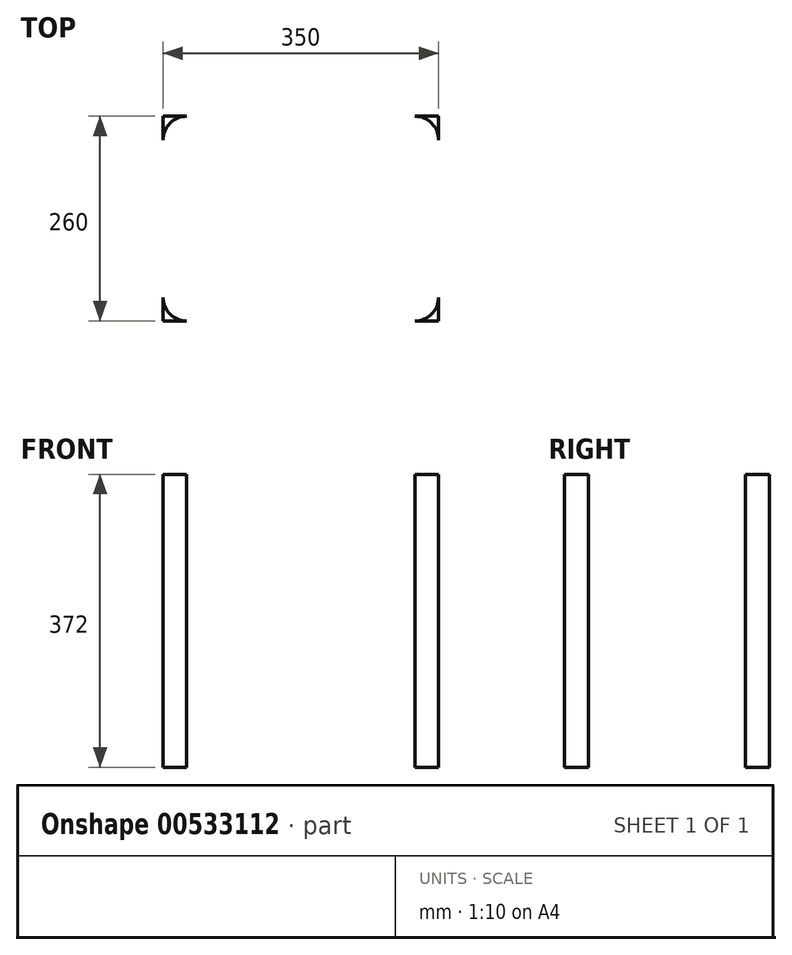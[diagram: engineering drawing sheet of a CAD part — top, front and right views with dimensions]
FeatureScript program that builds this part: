
annotation { "Feature Type Name" : "Feature", "Feature Type Description" : "" }
export const myFeature = defineFeature(function(context is Context, id is Id, definition is map)
    precondition{}
    {
        {
            var Q0;
            Q0=qCreatedBy(makeId("Top.planeOp"),FACE);
            var sketch = newSketch(context, id + "F0", { "sketchPlane" : qUnion([Q0])});
            skLineSegment(sketch, "E0.bottom", {"start": v(0, 260) * mm, "end": v(350, 260) * mm, "construction": true});
            skLineSegment(sketch, "E0.top", {"start": v(0, 0) * mm, "end": v(350, 0) * mm, "construction": true});
            skLineSegment(sketch, "E0.left", {"start": v(0, 260) * mm, "end": v(0, 0) * mm, "construction": true});
            skLineSegment(sketch, "E0.right", {"start": v(350, 260) * mm, "end": v(350, 0) * mm, "construction": true});
            skLineSegment(sketch, "E1.bottom", {"start": v(30, 260) * mm, "end": v(30, 260) * mm});
            skLineSegment(sketch, "E1.left", {"start": v(0, 230) * mm, "end": v(0, 230) * mm});
            skPoint(sketch, "E2.visualSharp", {"position": v(0, 260) * mm});
            skArc(sketch, "E2.filletArc", {"start": v(30, 260) * mm, "mid": v(8.79, 251.21) * mm, "end": v(0, 230) * mm});
            skLineSegment(sketch, "E3", {"start": v(175, 260) * mm, "end": v(175, 0) * mm, "construction": true});
            skLineSegment(sketch, "E4", {"start": v(0, 130) * mm, "end": v(350, 130) * mm, "construction": true});
            skLineSegment(sketch, "E5", {"start": v(30, 260) * mm, "end": v(0, 260) * mm});
            skLineSegment(sketch, "E6", {"start": v(0, 230) * mm, "end": v(0, 260) * mm});
            skLineSegment(sketch, "E7.MirrorCS", {"start": v(320, 260) * mm, "end": v(350, 260) * mm});
            skLineSegment(sketch, "E8.MirrorCS", {"start": v(350, 230) * mm, "end": v(350, 260) * mm});
            skPoint(sketch, "E9.MirrorP", {"position": v(350, 260) * mm});
            skArc(sketch, "E10.MirrorCS", {"start": v(320, 260) * mm, "mid": v(341.21, 251.21) * mm, "end": v(350, 230) * mm});
            skLineSegment(sketch, "E11.MirrorCS", {"start": v(350, 30) * mm, "end": v(350, 0) * mm});
            skPoint(sketch, "E12.MirrorP", {"position": v(0, 0) * mm});
            skArc(sketch, "E13.MirrorCS", {"start": v(320, 0) * mm, "mid": v(341.21, 8.79) * mm, "end": v(350, 30) * mm});
            skPoint(sketch, "E14.MirrorP", {"position": v(350, 0) * mm});
            skLineSegment(sketch, "E15.MirrorCS", {"start": v(320, 0) * mm, "end": v(350, 0) * mm});
            skLineSegment(sketch, "E16.MirrorCS", {"start": v(30, 0) * mm, "end": v(0, 0) * mm});
            skLineSegment(sketch, "E17.MirrorCS", {"start": v(0, 30) * mm, "end": v(0, 0) * mm});
            skArc(sketch, "E18.MirrorCS", {"start": v(30, 0) * mm, "mid": v(8.79, 8.79) * mm, "end": v(0, 30) * mm});
            skSolve(sketch);
        }
        {
            var Q0;
            Q0 = qSketchRegion(id + "F0", true);
            extrude(context, id + "F1", {"entities" : qUnion([Q0]), "depth" : 372 * mm, "offsetDistance" : 25 * mm});
        }
    });
